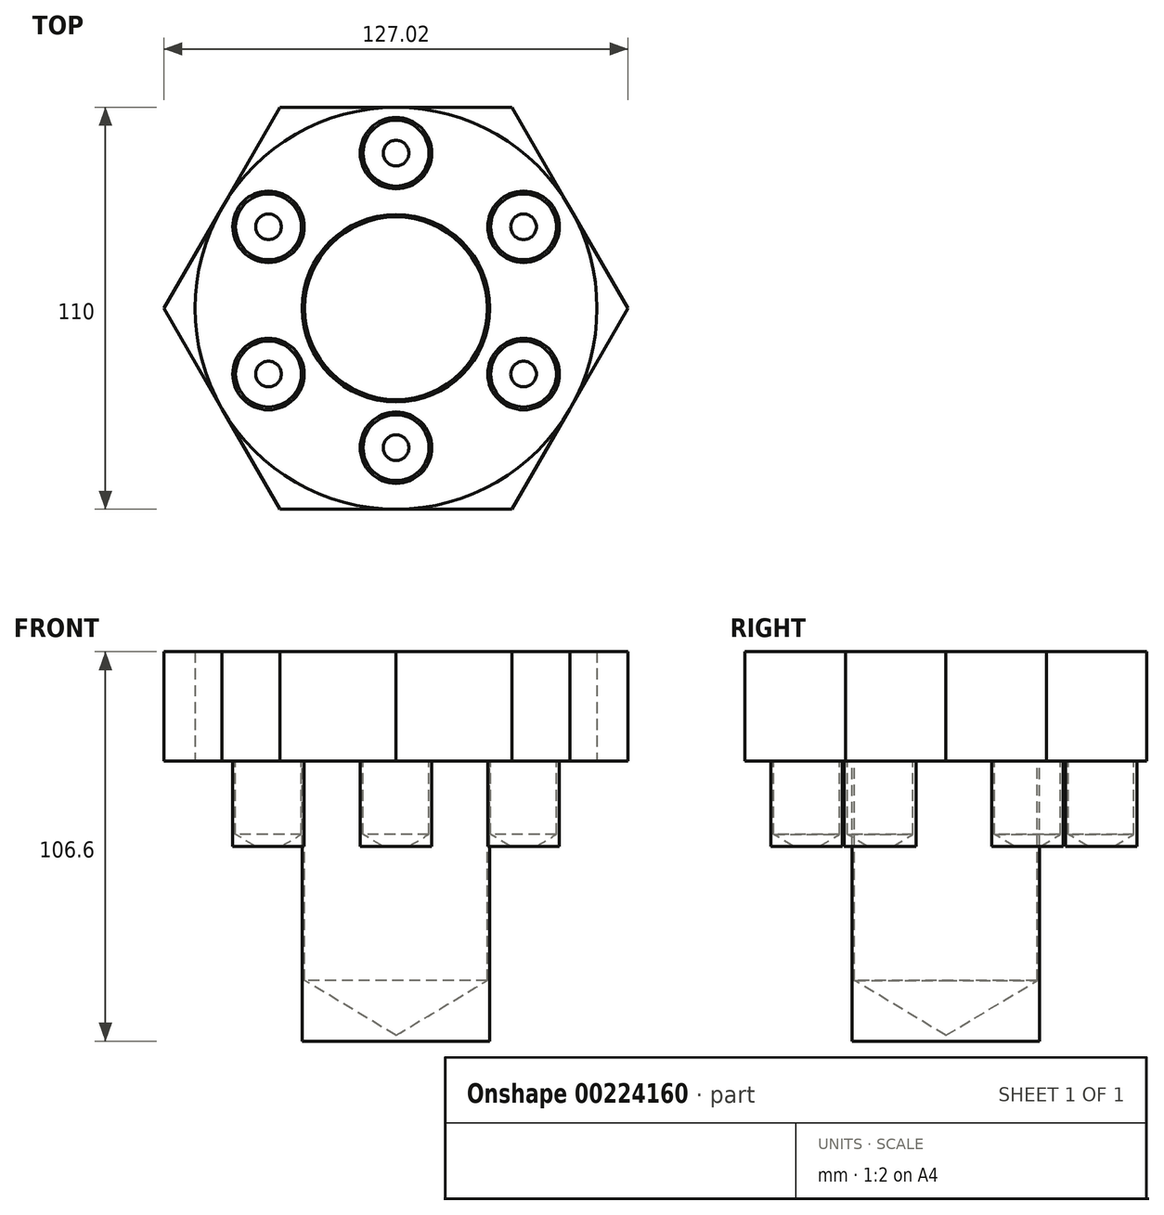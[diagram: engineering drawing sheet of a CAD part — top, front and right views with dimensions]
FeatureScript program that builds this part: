
annotation { "Feature Type Name" : "Feature", "Feature Type Description" : "" }
export const myFeature = defineFeature(function(context is Context, id is Id, definition is map)
    precondition{}
    {
        {
            var Q0;
            Q0=qCreatedBy(makeId("Top.planeOp"),FACE);
            var sketch = newSketch(context, id + "F0", { "sketchPlane" : qUnion([Q0])});
            skCircle(sketch, "E0", {"center": v(0, -2.15) * mm, "radius": 55 * mm});
            skCircle(sketch, "E1.cCircle", {"center": v(0, -2.15) * mm, "radius": 55 * mm, "construction": true});
            skLineSegment(sketch, "E1.0", {"start": v(-31.75, 52.85) * mm, "end": v(31.75, 52.85) * mm});
            skLineSegment(sketch, "E1.1", {"start": v(31.75, 52.85) * mm, "end": v(63.5, -2.15) * mm});
            skLineSegment(sketch, "E1.2", {"start": v(63.5, -2.15) * mm, "end": v(31.75, -57.15) * mm});
            skLineSegment(sketch, "E1.3", {"start": v(31.75, -57.15) * mm, "end": v(-31.75, -57.15) * mm});
            skLineSegment(sketch, "E1.4", {"start": v(-31.75, -57.15) * mm, "end": v(-63.5, -2.15) * mm});
            skLineSegment(sketch, "E1.5", {"start": v(-63.5, -2.15) * mm, "end": v(-31.75, 52.85) * mm});
            skPoint(sketch, "E1.0.midPoint", {"position": v(0, 52.85) * mm});
            skCircle(sketch, "E2", {"center": v(0, -2.15) * mm, "radius": 25.66 * mm});
            skSolve(sketch);
        }
        {
            var Q0;
            Q0=makeQuery(id+"F0.imprint","IMPRINT",FACE,{"disambiguationData":[TD([[makeQuery(id+"F0.imprint","IMPRINT",EDGE,{"derivedFrom":sQuery(id+"F0.wireOp",EDGE,"E2")}),1.0]])]});
            extrude(context, id + "F1", {"entities" : qUnion([Q0]), "oppositeDirection" : true, "depth" : 76.6 * mm});
        }
        {
            var Q0;
            Q0=sQuery(id+"F0.wireOp",VERTEX,"E0.center");
            var Q1;
            Q1=makeQuery(id+"F1.opExtrude","SWEPT_BODY",BODY,{"disambiguationData":[OSD([sQuery(id+"F0.wireOp",EDGE,"E2")])]});
            hole(context, id + "F2", {"style" : HoleStyle.SIMPLE, "endStyle" : HoleEndStyle.BLIND, "holeDiameter" : 50 * mm, "holeDepth" : 60 * mm, "locations" : qUnion([Q0]), "scope" : qUnion([Q1])});
        }
        {
            var Q0;
            {var subQ0=sQuery(id+"F0.wireOp",EDGE,"E1.0");var subQ1=sQuery(id+"F0.wireOp",EDGE,"E0");var subQ2=makeQuery(id+"F0.imprint","INTERSECT",VERTEX,{"derivedFrom":[subQ1,subQ0]});Q0=makeQuery(id+"F0.imprint","IMPRINT",FACE,{"disambiguationData":[TD([[makeQuery(id+"F0.imprint","IMPRINT",EDGE,{"disambiguationData":[TD([[subQ2,-1.0]])],"derivedFrom":subQ1}),-1.0]])]});}
            var Q1;
            {var subQ0=sQuery(id+"F0.wireOp",EDGE,"E1.5");var subQ1=sQuery(id+"F0.wireOp",EDGE,"E0");var subQ2=makeQuery(id+"F0.imprint","INTERSECT",VERTEX,{"derivedFrom":[subQ1,subQ0]});Q1=makeQuery(id+"F0.imprint","IMPRINT",FACE,{"disambiguationData":[TD([[makeQuery(id+"F0.imprint","IMPRINT",EDGE,{"disambiguationData":[TD([[subQ2,-1.0]])],"derivedFrom":subQ1}),-1.0]])]});}
            var Q2;
            {var subQ0=sQuery(id+"F0.wireOp",EDGE,"E1.4");var subQ1=sQuery(id+"F0.wireOp",EDGE,"E0");var subQ2=makeQuery(id+"F0.imprint","INTERSECT",VERTEX,{"derivedFrom":[subQ1,subQ0]});Q2=makeQuery(id+"F0.imprint","IMPRINT",FACE,{"disambiguationData":[TD([[makeQuery(id+"F0.imprint","IMPRINT",EDGE,{"disambiguationData":[TD([[subQ2,-1.0]])],"derivedFrom":subQ1}),-1.0]])]});}
            var Q3;
            {var subQ0=sQuery(id+"F0.wireOp",EDGE,"E1.3");var subQ1=sQuery(id+"F0.wireOp",EDGE,"E0");var subQ2=makeQuery(id+"F0.imprint","INTERSECT",VERTEX,{"derivedFrom":[subQ1,subQ0]});Q3=makeQuery(id+"F0.imprint","IMPRINT",FACE,{"disambiguationData":[TD([[makeQuery(id+"F0.imprint","IMPRINT",EDGE,{"disambiguationData":[TD([[subQ2,-1.0]])],"derivedFrom":subQ1}),-1.0]])]});}
            var Q4;
            {var subQ0=sQuery(id+"F0.wireOp",EDGE,"E1.0");var subQ1=sQuery(id+"F0.wireOp",EDGE,"E0");var subQ2=makeQuery(id+"F0.imprint","INTERSECT",VERTEX,{"derivedFrom":[subQ1,subQ0]});Q4=makeQuery(id+"F0.imprint","IMPRINT",FACE,{"disambiguationData":[TD([[makeQuery(id+"F0.imprint","IMPRINT",EDGE,{"disambiguationData":[TD([[subQ2,1.0]])],"derivedFrom":subQ1}),-1.0]])]});}
            var Q5;
            {var subQ0=sQuery(id+"F0.wireOp",EDGE,"E1.1");var subQ1=sQuery(id+"F0.wireOp",EDGE,"E0");var subQ2=makeQuery(id+"F0.imprint","INTERSECT",VERTEX,{"derivedFrom":[subQ1,subQ0]});Q5=makeQuery(id+"F0.imprint","IMPRINT",FACE,{"disambiguationData":[TD([[makeQuery(id+"F0.imprint","IMPRINT",EDGE,{"disambiguationData":[TD([[subQ2,1.0]])],"derivedFrom":subQ1}),-1.0]])]});}
            extrude(context, id + "F3", {"entities" : qUnion([Q0, Q1, Q2, Q3, Q4, Q5]), "depth" : 30 * mm});
        }
        {
            var Q0;
            Q0=makeQuery(id+"F0.imprint","IMPRINT",FACE,{"disambiguationData":[TD([[makeQuery(id+"F0.imprint","IMPRINT",EDGE,{"derivedFrom":sQuery(id+"F0.wireOp",EDGE,"E2")}),-1.0]])]});
            var sketch = newSketch(context, id + "F4", { "sketchPlane" : qUnion([Q0])});
            skCircle(sketch, "E3", {"center": v(0, 40.3) * mm, "radius": 9.8 * mm});
            skCircle(sketch, "E4.1.0", {"center": v(-34.9, 20.15) * mm, "radius": 9.8 * mm});
            skCircle(sketch, "E4.2.0", {"center": v(-34.9, -20.15) * mm, "radius": 9.8 * mm});
            skCircle(sketch, "E4.3.0", {"center": v(0, -40.3) * mm, "radius": 9.8 * mm});
            skCircle(sketch, "E4.4.0", {"center": v(34.9, -20.15) * mm, "radius": 9.8 * mm});
            skCircle(sketch, "E4.5.0", {"center": v(34.9, 20.15) * mm, "radius": 9.8 * mm});
            skPoint(sketch, "E4.center", {"position": v(0, 0) * mm});
            skSolve(sketch);
        }
        {
            var Q0;
            Q0 = qSketchRegion(id + "F4", true);
            extrude(context, id + "F5", {"entities" : qUnion([Q0]), "oppositeDirection" : true, "depth" : 23.3 * mm});
        }
        {
            var Q0;
            Q0=sQuery(id+"F4.wireOp",VERTEX,"E4.1.0.center");
            var Q1;
            Q1=sQuery(id+"F4.wireOp",VERTEX,"E3.center");
            var Q2;
            Q2=sQuery(id+"F4.wireOp",VERTEX,"E4.5.0.center");
            var Q3;
            Q3=sQuery(id+"F4.wireOp",VERTEX,"E4.4.0.center");
            var Q4;
            Q4=sQuery(id+"F4.wireOp",VERTEX,"E4.3.0.center");
            var Q5;
            Q5=sQuery(id+"F4.wireOp",VERTEX,"E4.2.0.center");
            var Q6;
            Q6=makeQuery(id+"F5.opExtrude","SWEPT_BODY",BODY,{"disambiguationData":[OSD([sQuery(id+"F4.wireOp",EDGE,"E4.1.0")])]});
            var Q7;
            Q7=makeQuery(id+"F5.opExtrude","SWEPT_BODY",BODY,{"disambiguationData":[OSD([sQuery(id+"F4.wireOp",EDGE,"E3")])]});
            var Q8;
            Q8=makeQuery(id+"F5.opExtrude","SWEPT_BODY",BODY,{"disambiguationData":[OSD([sQuery(id+"F4.wireOp",EDGE,"E4.5.0")])]});
            var Q9;
            Q9=makeQuery(id+"F5.opExtrude","SWEPT_BODY",BODY,{"disambiguationData":[OSD([sQuery(id+"F4.wireOp",EDGE,"E4.4.0")])]});
            var Q10;
            Q10=makeQuery(id+"F5.opExtrude","SWEPT_BODY",BODY,{"disambiguationData":[OSD([sQuery(id+"F4.wireOp",EDGE,"E4.3.0")])]});
            var Q11;
            Q11=makeQuery(id+"F5.opExtrude","SWEPT_BODY",BODY,{"disambiguationData":[OSD([sQuery(id+"F4.wireOp",EDGE,"E4.2.0")])]});
            hole(context, id + "F6", {"style" : HoleStyle.SIMPLE, "endStyle" : HoleEndStyle.BLIND, "holeDiameter" : 18 * mm, "holeDepth" : 20 * mm, "locations" : qUnion([Q0, Q1, Q2, Q3, Q4, Q5]), "scope" : qUnion([Q6, Q7, Q8, Q9, Q10, Q11])});
        }
    });
